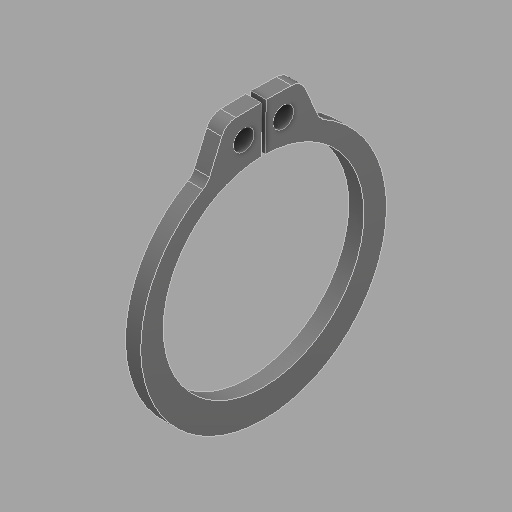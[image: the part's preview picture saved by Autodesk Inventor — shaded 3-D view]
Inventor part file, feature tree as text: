
AUTODESK INVENTOR PART (.ipt)
format: ipt  version: 2024.2 (Build 282272000, 272)  size: 110,592 bytes
history: native  units: in
note: dims shown in document units (in); Inventor stores cm internally (conversion verified against a paired STEP export)
features: fillet x1
ambient origin geometry x8: Origin, YZ Plane, XZ Plane, XY Plane, X Axis, Y Axis, Z Axis, Center Point
bodies: Solid1 (feature_tree)
feature tree (1):
  fillet  "Fillet1"  [1 undecoded]
note: 1 required parameter value undecoded (feature->parameter linkage not recoverable at this tier; creation-order binding heuristic only, values carry confidence <= 0.55)
